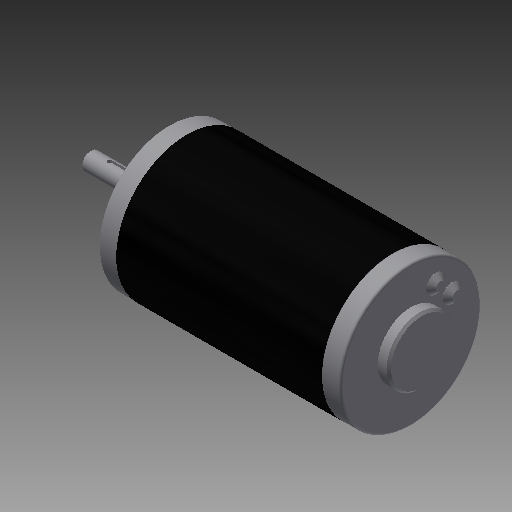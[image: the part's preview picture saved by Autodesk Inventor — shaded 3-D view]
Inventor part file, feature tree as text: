
AUTODESK INVENTOR PART (.ipt)
format: ipt  version: 2019 (Build 230136000, 136)  size: 174,592 bytes
history: native  units: in
note: dims shown in document units (in); Inventor stores cm internally (conversion verified against a paired STEP export)
features: chamfer x1, other x1, imported_body x1
ambient origin geometry x8: Origin, YZ Plane, XZ Plane, XY Plane, X Axis, Y Axis, Z Axis, Center Point
bodies: Body1 (feature_tree)
feature tree (3):
  chamfer  "Chamfer3"  [1 undecoded]
  other  "CIM Motor1"
  imported_body  "Base1"
note: 1 required parameter value undecoded (feature->parameter linkage not recoverable at this tier; creation-order binding heuristic only, values carry confidence <= 0.55)
